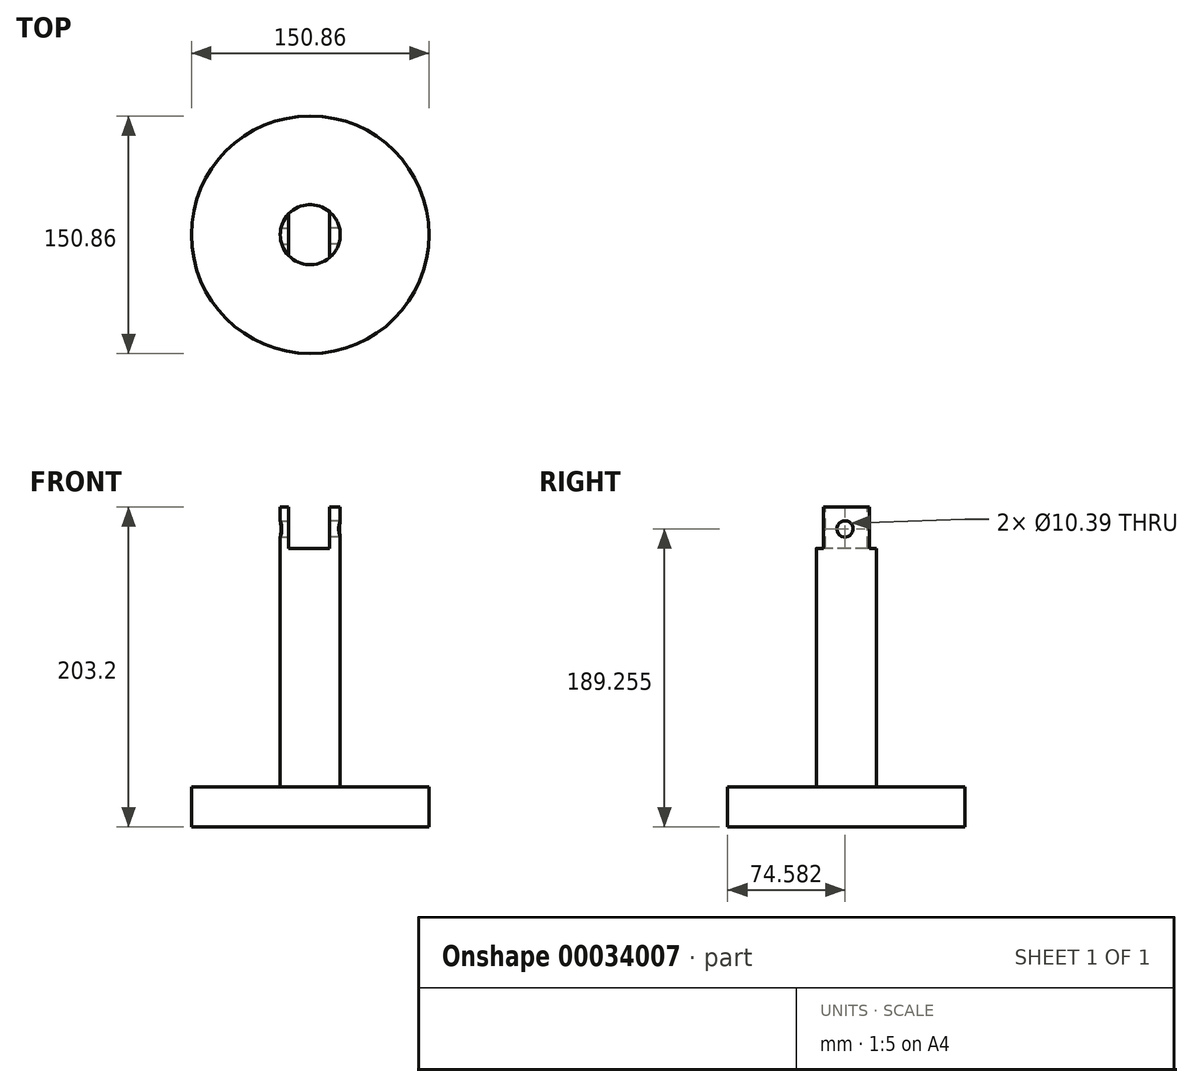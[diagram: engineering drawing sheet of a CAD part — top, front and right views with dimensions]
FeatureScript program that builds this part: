
annotation { "Feature Type Name" : "Feature", "Feature Type Description" : "" }
export const myFeature = defineFeature(function(context is Context, id is Id, definition is map)
    precondition{}
    {
        {
            var Q0;
            Q0=qCreatedBy(makeId("Top.planeOp"),FACE);
            var sketch = newSketch(context, id + "F0", { "sketchPlane" : qUnion([Q0])});
            skCircle(sketch, "E0", {"center": v(0, 0) * mm, "radius": 75.43 * mm});
            skSolve(sketch);
        }
        {
            var Q0;
            Q0 = qSketchRegion(id + "F0", true);
            extrude(context, id + "F1", {"entities" : qUnion([Q0]), "depth" : 25.4 * mm});
        }
        {
            var Q0;
            Q0=qCreatedBy(makeId("Top.planeOp"),FACE);
            var sketch = newSketch(context, id + "F10", { "sketchPlane" : qUnion([Q0])});
            skCircle(sketch, "E1", {"center": v(0, 0) * mm, "radius": 19.05 * mm});
            skSolve(sketch);
        }
        {
            var Q0;
            Q0=makeQuery(id+"F10.imprint","IMPRINT",FACE,{"disambiguationData":[TD([[makeQuery(id+"F10.imprint","IMPRINT",EDGE,{"derivedFrom":sQuery(id+"F10.wireOp",EDGE,"E1")}),1.0]])]});
            var Q1;
            Q1 = qSketchRegion(id + "F3", true);
            extrude(context, id + "F2", {"entities" : qUnion([Q0, Q1]), "operationType" : NewBodyOperationType.ADD, "depth" : 203.2 * mm});
        }
        {
            var Q0;
            Q0=makeQuery(id+"F2.opExtrude","CAP_FACE",FACE,{"disambiguationData":[OSD([sQuery(id+"F10.wireOp",EDGE,"E1")])],"isStart":false});
            var sketch = newSketch(context, id + "F3", { "sketchPlane" : qUnion([Q0])});
            skLineSegment(sketch, "E2.bottom", {"start": v(-13.61, 26.5) * mm, "end": v(12.24, 26.5) * mm});
            skLineSegment(sketch, "E2.top", {"start": v(-13.61, -29.48) * mm, "end": v(12.24, -29.48) * mm});
            skLineSegment(sketch, "E2.left", {"start": v(-13.61, 26.5) * mm, "end": v(-13.61, -29.48) * mm});
            skLineSegment(sketch, "E2.right", {"start": v(12.24, 26.5) * mm, "end": v(12.24, -29.48) * mm});
            skSolve(sketch);
        }
        {
            var Q0;
            {var subQ0=makeQuery(id+"F2.opExtrude","CAP_EDGE",EDGE,{"disambiguationData":[OSD([sQuery(id+"F10.wireOp",EDGE,"E1")])],"isStart":false});var subQ3=sQuery(id+"F3.wireOp",EDGE,"E2.left");var subQ6=makeQuery(id+"F3.imprint","INTERSECT",VERTEX,{"disambiguationData":[OD(0.0)],"derivedFrom":[subQ0,subQ3]});Q0=makeQuery(id+"F3.imprint","IMPRINT",FACE,{"disambiguationData":[TD([[makeQuery(id+"F3.imprint","IMPRINT",EDGE,{"disambiguationData":[TD([[subQ6,-1.0]])],"derivedFrom":subQ3}),1.0]])]});}
            extrude(context, id + "F4", {"entities" : qUnion([Q0]), "operationType" : NewBodyOperationType.REMOVE, "oppositeDirection" : true, "depth" : 26.26 * mm});
        }
        {
            var Q0;
            Q0=makeQuery(id+"F4.boolean.opBoolean","COPY",FACE,{"derivedFrom":makeQuery(id+"F4.opExtrude","SWEPT_FACE",FACE,{"disambiguationData":[OSD([sQuery(id+"F3.wireOp",EDGE,"E2.left")])]})});
            var sketch = newSketch(context, id + "F5", { "sketchPlane" : qUnion([Q0])});
            skCircle(sketch, "E3", {"center": v(-189.92, 0) * mm, "radius": 5.34 * mm});
            skSolve(sketch);
        }
        {
            var Q0;
            Q0 = qSketchRegion(id + "F5", true);
            extrude(context, id + "F6", {"entities" : qUnion([Q0]), "operationType" : NewBodyOperationType.REMOVE, "oppositeDirection" : true, "depth" : 25.4 * mm});
        }
        {
            var Q0;
            Q0=makeQuery(id+"F4.boolean.opBoolean","COPY",FACE,{"derivedFrom":makeQuery(id+"F4.opExtrude","SWEPT_FACE",FACE,{"disambiguationData":[OSD([sQuery(id+"F3.wireOp",EDGE,"E2.left")])]})});
            var sketch = newSketch(context, id + "F7", { "sketchPlane" : qUnion([Q0])});
            skPoint(sketch, "E4.centerSnap0", {"position": v(0, 176.94) * mm});
            skCircle(sketch, "E5", {"center": v(-0.85, 189.26) * mm, "radius": 5.2 * mm});
            skSolve(sketch);
        }
        {
            var Q0;
            Q0=makeQuery(id+"F7.imprint","IMPRINT",FACE,{"disambiguationData":[TD([[makeQuery(id+"F7.imprint","IMPRINT",EDGE,{"derivedFrom":sQuery(id+"F7.wireOp",EDGE,"E5")}),1.0]])]});
            extrude(context, id + "F8", {"entities" : qUnion([Q0]), "operationType" : NewBodyOperationType.REMOVE, "oppositeDirection" : true, "depth" : 22.4 * mm});
        }
        {
            var Q0;
            Q0=makeQuery(id+"F7.imprint","IMPRINT",FACE,{"disambiguationData":[TD([[makeQuery(id+"F7.imprint","IMPRINT",EDGE,{"derivedFrom":sQuery(id+"F7.wireOp",EDGE,"E5")}),1.0]])]});
            extrude(context, id + "F9", {"entities" : qUnion([Q0]), "operationType" : NewBodyOperationType.REMOVE, "depth" : 72.39 * mm});
        }
    });
